# Revit family: Supply_Kit-Watercloset-Waterworks-Universal-Angle
name_source: partatom
category: Plumbing Fixtures
revit_build: Autodesk Revit MEP 2014 (Build: 20140709_2115(x64)
units: mm (PartAtom-declared; Revit-internal decimal feet)

## types (32) — shared parameters
ADA Compliant = Yes
Assembly Code = D2010
CW Connection = Yes
Certification IAPMO = Yes
Certification State of MA = Yes
Certification cUPC = Yes
Cold Water Diameter = 0' - 0 1/2"
Cold Water Outlet Connection = Outlet - Compression
Default Elevation = 2' - 10"
HW Connection = No
Keynote = 22 40 00
Manufacturer = Waterworks
Outlet Connection Diameter = 0' - 0 3/8"
Pressure = 45.00 psi
Product Documentation Link = http://assets.waterworks.com
Product Page URL = http://www.waterworks.com
URL = http://www.waterworks.com
Vent Connection = No
Version = 2014 - v1.0a
Warranty = http://www.waterworks.com
Waste Connection = No
Water Pressure = Max: 85psi / Min: 20psi / Recommended: 45psi
‌Installation Requirements or Notes = Additional made-to-order finish options are available in 12 weeks from purchase
zero-valued in all types: CWFU, HWFU, WFU

## per-type parameters (varying)
| type | Code Compliance | Cold Water Inlet Connection | Constraint | ControlM | Description | Finish | Length | Long Trim | Model | Model SKU | Product Name | Short Trim |
| Compression - Antique Brass | Code # FDMS31: ASME A112.18.1 / CSA B125.1, IAPMO, State of MA | Inlet - Compression | 1 | 1 | Universal Angle Watercloset Supply Kits 1/2” Compression x 3/8” O.D. Compression in Antique Brass | Metal - Waterworks - Antique Brass | 0' - 2 3/8" | No | UNMS31 | 26-98128-10038 | Universal Angle Watercloset Supply Kits 1/2” Compression x 3/8” O.D. Compression in Antique Brass | Yes |
| Compression - Antique Copper | Code # FDMS31: ASME A112.18.1 / CSA B125.1, IAPMO, State of MA | Inlet - Compression | 1 | 2 | Universal Angle Watercloset Supply Kits 1/2” Compression x 3/8” O.D. Compression in Antique Copper | Metal - Waterworks - Antique Copper | 0' - 2 3/8" | No | UNMS31 | 26-94704-48892 | Universal Angle Watercloset Supply Kits 1/2” Compression x 3/8” O.D. Compression in Antique Copper | Yes |
| Compression - Architectural Bronze | Code # FDMS31: ASME A112.18.1 / CSA B125.1, IAPMO, State of MA | Inlet - Compression | 1 | 3 | Universal Angle Watercloset Supply Kits 1/2” Compression x 3/8” O.D. Compression in Architectural Bronze | Metal - Waterworks - Architectural Bronze | 0' - 2 3/8" | No | UNMS31 | 26-91500-49692 | Universal Angle Watercloset Supply Kits 1/2” Compression x 3/8” O.D. Compression in Architectural Bronze | Yes |
| Compression - Burnished Brass | Code # FDMS31: ASME A112.18.1 / CSA B125.1, IAPMO, State of MA | Inlet - Compression | 1 | 4 | Universal Angle Watercloset Supply Kits 1/2” Compression x 3/8” O.D. Compression in Burnished Brass | Metal - Waterworks - Burnished Brass | 0' - 2 3/8" | No | UNMS31 | 26-75215-59631 | Universal Angle Watercloset Supply Kits 1/2” Compression x 3/8” O.D. Compression in Burnished Brass | Yes |
| Compression - Burnished Nickel | Code # FDMS31: ASME A112.18.1 / CSA B125.1, IAPMO, State of MA | Inlet - Compression | 1 | 5 | Universal Angle Watercloset Supply Kits 1/2” Compression x 3/8” O.D. Compression in Burnished Nickel | Metal - Waterworks - Burnished Nickel | 0' - 2 3/8" | No | UNMS31 | 26-40591-17287 | Universal Angle Watercloset Supply Kits 1/2” Compression x 3/8” O.D. Compression in Burnished Nickel | Yes |
| Compression - Carbon | Code # FDMS31: ASME A112.18.1 / CSA B125.1, IAPMO, State of MA | Inlet - Compression | 1 | 6 | Universal Angle Watercloset Supply Kits 1/2” Compression x 3/8” O.D. Compression in Carbon | Metal - Waterworks - Carbon | 0' - 2 3/8" | No | UNMS31 | 26-79504-86116 | Universal Angle Watercloset Supply Kits 1/2” Compression x 3/8” O.D. Compression in Carbon | Yes |
| Compression - Chrome | Code # FDMS31: ASME A112.18.1 / CSA B125.1, IAPMO, State of MA | Inlet - Compression | 1 | 7 | Universal Angle Watercloset Supply Kits 1/2” Compression x 3/8” O.D. Compression in Chrome | Metal - Waterworks - Chrome | 0' - 2 3/8" | No | UNMS31 | 26-94383-34073 | Universal Angle Watercloset Supply Kits 1/2” Compression x 3/8” O.D. Compression in Chrome | Yes |
| Compression - Gold | Code # FDMS31: ASME A112.18.1 / CSA B125.1, IAPMO, State of MA | Inlet - Compression | 1 | 8 | Universal Angle Watercloset Supply Kits 1/2” Compression x 3/8” O.D. Compression in Gold | Metal - Waterworks - Gold | 0' - 2 3/8" | No | UNMS31 | 26-85701-08009 | Universal Angle Watercloset Supply Kits 1/2” Compression x 3/8” O.D. Compression in Gold | Yes |
| Compression - Matte Gold | Code # FDMS31: ASME A112.18.1 / CSA B125.1, IAPMO, State of MA | Inlet - Compression | 1 | 9 | Universal Angle Watercloset Supply Kits 1/2” Compression x 3/8” O.D. Compression in Matte Gold | Metal - Waterworks - Matte Gold | 0' - 2 3/8" | No | UNMS31 | 26-47688-23317 | Universal Angle Watercloset Supply Kits 1/2” Compression x 3/8” O.D. Compression in Matte Gold | Yes |
| Compression - Matte Nickel | Code # FDMS31: ASME A112.18.1 / CSA B125.1, IAPMO, State of MA | Inlet - Compression | 1 | 10 | Universal Angle Watercloset Supply Kits 1/2” Compression x 3/8” O.D. Compression in Matte Nickel | Metal - Waterworks - Matte Nickel | 0' - 2 3/8" | No | UNMS31 | 26-64024-09915 | Universal Angle Watercloset Supply Kits 1/2” Compression x 3/8” O.D. Compression in Matte Nickel | Yes |
| Compression - Nickel | Code # FDMS31: ASME A112.18.1 / CSA B125.1, IAPMO, State of MA | Inlet - Compression | 1 | 11 | Universal Angle Watercloset Supply Kits 1/2” Compression x 3/8” O.D. Compression in Nickel | Metal - Waterworks - Nickel | 0' - 2 3/8" | No | UNMS31 | 26-94389-50764 | Universal Angle Watercloset Supply Kits 1/2” Compression x 3/8” O.D. Compression in Nickel | Yes |
| Compression - Pewter | Code # FDMS31: ASME A112.18.1 / CSA B125.1, IAPMO, State of MA | Inlet - Compression | 1 | 12 | Universal Angle Watercloset Supply Kits 1/2” Compression x 3/8” O.D. Compression in Pewter | Metal - Waterworks - Pewter | 0' - 2 3/8" | No | UNMS31 | 26-53021-63245 | Universal Angle Watercloset Supply Kits 1/2” Compression x 3/8” O.D. Compression in Pewter | Yes |
| Compression - Shiny Copper | Code # FDMS31: ASME A112.18.1 / CSA B125.1, IAPMO, State of MA | Inlet - Compression | 1 | 13 | Universal Angle Watercloset Supply Kits 1/2” Compression x 3/8” O.D. Compression in Shiny Copper | Metal - Waterworks - Shiny Copper | 0' - 2 3/8" | No | UNMS31 | 26-52522-07735 | Universal Angle Watercloset Supply Kits 1/2” Compression x 3/8” O.D. Compression in Shiny Copper | Yes |
| Compression - Sovereign | Code # FDMS31: ASME A112.18.1 / CSA B125.1, IAPMO, State of MA | Inlet - Compression | 1 | 14 | Universal Angle Watercloset Supply Kits 1/2” Compression x 3/8” O.D. Compression in Sovereign | Metal - Waterworks - Sovereign | 0' - 2 3/8" | No | UNMS31 | 26-82545-86021 | Universal Angle Watercloset Supply Kits 1/2” Compression x 3/8” O.D. Compression in Sovereign | Yes |
| Compression - Unfinished | Code # FDMS31: ASME A112.18.1 / CSA B125.1, IAPMO, State of MA | Inlet - Compression | 1 | 15 | Universal Angle Watercloset Supply Kits 1/2” Compression x 3/8” O.D. Compression in Unfinished | Metal - Waterworks - Unfinished | 0' - 2 3/8" | No | UNMS31 | 26-50209-75321 | Universal Angle Watercloset Supply Kits 1/2” Compression x 3/8” O.D. Compression in Unfinished | Yes |
| Compression - Unlacquered Brass | Code # FDMS31: ASME A112.18.1 / CSA B125.1, IAPMO, State of MA | Inlet - Compression | 1 | 16 | Universal Angle Watercloset Supply Kits 1/2” Compression x 3/8” O.D. Compression in Unlacquered Brass | Metal - Waterworks - Unlacquered Brass | 0' - 2 3/8" | No | UNMS31 | 26-20730-88148 | Universal Angle Watercloset Supply Kits 1/2” Compression x 3/8” O.D. Compression in Unlacquered Brass | Yes |
| Compression - Vintage Brass | Code # FDMS31: ASME A112.18.1 / CSA B125.1, IAPMO, State of MA | Inlet - Compression | 1 | 17 | Universal Angle Watercloset Supply Kits 1/2” Compression x 3/8” O.D. Compression in Vintage Brass | Metal - Waterworks - Vintage Brass | 0' - 2 3/8" | No | UNMS31 | 26-80070-28824 | Universal Angle Watercloset Supply Kits 1/2” Compression x 3/8” O.D. Compression in Vintage Brass | Yes |
| Sweat - Antique Brass | Code # FDMS33: ASME A112.18.1 / CSA B125.1, IAPMO, State of MA | Inlet - Sweat | 2 | 1 | Universal Angle Watercloset Supply Kits 1/2” Sweat x 3/8” O.D. Compression in Antique Brass | Metal - Waterworks - Antique Brass | 0' - 2 3/16" | Yes | UNMS33 | 26-05712-82175 | Universal Angle Watercloset Supply Kits 1/2” Sweat x 3/8” O.D. Compression in Antique Brass | No |
| Sweat - Antique Copper | Code # FDMS33: ASME A112.18.1 / CSA B125.1, IAPMO, State of MA | Inlet - Sweat | 2 | 2 | Universal Angle Watercloset Supply Kits 1/2” Sweat x 3/8” O.D. Compression in Antique Copper | Metal - Waterworks - Antique Copper | 0' - 2 3/16" | Yes | UNMS33 | 26-62939-38577 | Universal Angle Watercloset Supply Kits 1/2” Sweat x 3/8” O.D. Compression in Antique Copper | No |
| Sweat - Architectural Bronze | Code # FDMS33: ASME A112.18.1 / CSA B125.1, IAPMO, State of MA | Inlet - Sweat | 2 | 3 | Universal Angle Watercloset Supply Kits 1/2” Sweat x 3/8” O.D. Compression in Architectural Bronze | Metal - Waterworks - Architectural Bronze | 0' - 2 3/16" | Yes | UNMS33 | 26-67944-86272 | Universal Angle Watercloset Supply Kits 1/2” Sweat x 3/8” O.D. Compression in Architectural Bronze | No |
| Sweat - Burnished Brass | Code # FDMS33: ASME A112.18.1 / CSA B125.1, IAPMO, State of MA | Inlet - Sweat | 2 | 4 | Universal Angle Watercloset Supply Kits 1/2” Sweat x 3/8” O.D. Compression in Burnished Brass | Metal - Waterworks - Burnished Brass | 0' - 2 3/16" | Yes | UNMS33 | 26-81442-82545 | Universal Angle Watercloset Supply Kits 1/2” Sweat x 3/8” O.D. Compression in Burnished Brass | No |
| Sweat - Carbon | Code # FDMS33: ASME A112.18.1 / CSA B125.1, IAPMO, State of MA | Inlet - Sweat | 2 | 5 | Universal Angle Watercloset Supply Kits 1/2” Sweat x 3/8” O.D. Compression in Carbon | Metal - Waterworks - Carbon | 0' - 2 3/16" | Yes | UNMS33 | 26-34765-26806 | Universal Angle Watercloset Supply Kits 1/2” Sweat x 3/8” O.D. Compression in Carbon | No |
| Sweat - Chrome | Code # FDMS33: ASME A112.18.1 / CSA B125.1, IAPMO, State of MA | Inlet - Sweat | 2 | 6 | Universal Angle Watercloset Supply Kits 1/2” Sweat x 3/8” O.D. Compression in Chrome | Metal - Waterworks - Chrome | 0' - 2 3/16" | Yes | UNMS33 | 26-22145-74198 | Universal Angle Watercloset Supply Kits 1/2” Sweat x 3/8” O.D. Compression in Chrome | No |
| Sweat - Gold | Code # FDMS33: ASME A112.18.1 / CSA B125.1, IAPMO, State of MA | Inlet - Sweat | 2 | 7 | Universal Angle Watercloset Supply Kits 1/2” Sweat x 3/8” O.D. Compression in Gold | Metal - Waterworks - Gold | 0' - 2 3/16" | Yes | UNMS33 | 26-41698-21325 | Universal Angle Watercloset Supply Kits 1/2” Sweat x 3/8” O.D. Compression in Gold | No |
| Sweat - Matte Gold | Code # FDMS33: ASME A112.18.1 / CSA B125.1, IAPMO, State of MA | Inlet - Sweat | 2 | 8 | Universal Angle Watercloset Supply Kits 1/2” Sweat x 3/8” O.D. Compression in Matte Gold | Metal - Waterworks - Matte Gold | 0' - 2 3/16" | Yes | UNMS33 | 26-48377-83750 | Universal Angle Watercloset Supply Kits 1/2” Sweat x 3/8” O.D. Compression in Matte Gold | No |
| Sweat - Matte Nickel | Code # FDMS33: ASME A112.18.1 / CSA B125.1, IAPMO, State of MA | Inlet - Sweat | 2 | 9 | Universal Angle Watercloset Supply Kits 1/2” Sweat x 3/8” O.D. Compression in Matte Nickel | Metal - Waterworks - Matte Nickel | 0' - 2 3/16" | Yes | UNMS33 | 26-17450-04785 | Universal Angle Watercloset Supply Kits 1/2” Sweat x 3/8” O.D. Compression in Matte Nickel | No |
| Sweat - Nickel | Code # FDMS33: ASME A112.18.1 / CSA B125.1, IAPMO, State of MA | Inlet - Sweat | 2 | 10 | Universal Angle Watercloset Supply Kits 1/2” Sweat x 3/8” O.D. Compression in Nickel | Metal - Waterworks - Nickel | 0' - 2 3/16" | Yes | UNMS33 | 26-32227-72857 | Universal Angle Watercloset Supply Kits 1/2” Sweat x 3/8” O.D. Compression in Nickel | No |
| Sweat - Pewter | Code # FDMS33: ASME A112.18.1 / CSA B125.1, IAPMO, State of MA | Inlet - Sweat | 2 | 11 | Universal Angle Watercloset Supply Kits 1/2” Sweat x 3/8” O.D. Compression in Pewter | Metal - Waterworks - Pewter | 0' - 2 3/16" | Yes | UNMS33 | 26-38601-89249 | Universal Angle Watercloset Supply Kits 1/2” Sweat x 3/8” O.D. Compression in Pewter | No |
| Sweat - Shiny Copper | Code # FDMS33: ASME A112.18.1 / CSA B125.1, IAPMO, State of MA | Inlet - Sweat | 2 | 12 | Universal Angle Watercloset Supply Kits 1/2” Sweat x 3/8” O.D. Compression in Shiny Copper | Metal - Waterworks - Shiny Copper | 0' - 2 3/16" | Yes | UNMS33 | 26-69594-07291 | Universal Angle Watercloset Supply Kits 1/2” Sweat x 3/8” O.D. Compression in Shiny Copper | No |
| Sweat - Sovereign | Code # FDMS33: ASME A112.18.1 / CSA B125.1, IAPMO, State of MA | Inlet - Sweat | 2 | 13 | Universal Angle Watercloset Supply Kits 1/2” Sweat x 3/8” O.D. Compression in Sovereign | Metal - Waterworks - Sovereign | 0' - 2 3/16" | Yes | UNMS33 | 26-21722-80402 | Universal Angle Watercloset Supply Kits 1/2” Sweat x 3/8” O.D. Compression in Sovereign | No |
| Sweat - Unlacquered Brass | Code # FDMS33: ASME A112.18.1 / CSA B125.1, IAPMO, State of MA | Inlet - Sweat | 2 | 14 | Universal Angle Watercloset Supply Kits 1/2” Sweat x 3/8” O.D. Compression in Unlacquered Brass | Metal - Waterworks - Unlacquered Brass | 0' - 2 3/16" | Yes | UNMS33 | 26-01799-84264 | Universal Angle Watercloset Supply Kits 1/2” Sweat x 3/8” O.D. Compression in Unlacquered Brass | No |
| Sweat - Vintage Brass | Code # FDMS33: ASME A112.18.1 / CSA B125.1, IAPMO, State of MA | Inlet - Sweat | 2 | 15 | Universal Angle Watercloset Supply Kits 1/2” Sweat x 3/8” O.D. Compression in Vintage Brass | Metal - Waterworks - Vintage Brass | 0' - 2 3/16" | Yes | UNMS33 | 26-77155-91201 | Universal Angle Watercloset Supply Kits 1/2” Sweat x 3/8” O.D. Compression in Vintage Brass | No |

## geometry (parser evidence)
native form markers: Sweep x1
no freeform markers — native parametric forms only
